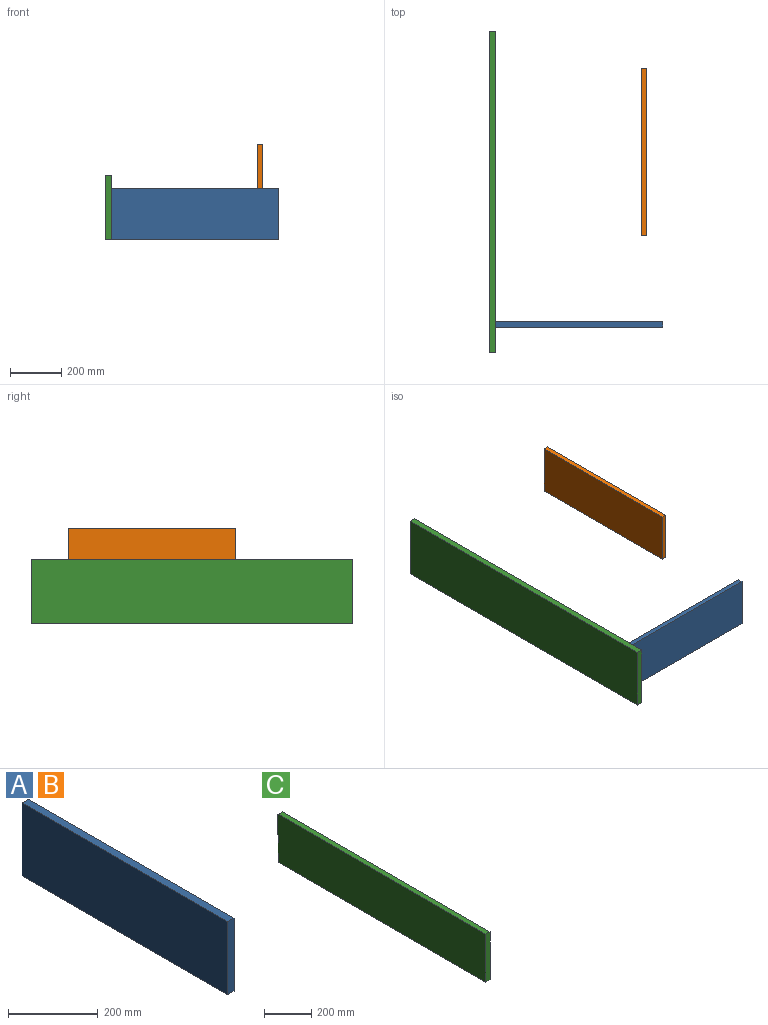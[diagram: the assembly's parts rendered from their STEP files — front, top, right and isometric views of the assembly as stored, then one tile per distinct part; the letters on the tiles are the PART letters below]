
ASSEMBLY  parts=3 mates=1
PART A: 6 faces, bbox 20x650x200 mm
  f0: plane 650x200mm, normal (-1,0,0), area 130000mm2, adj f1,f3,f4,f5
  f1: plane 650x20mm, normal (0,0,-1), area 13000mm2, adj f0,f2,f4,f5
  f2: plane 650x200mm, normal (1,0,0), area 130000mm2, adj f1,f3,f4,f5
  f3: plane 650x20mm, normal (0,0,1), area 13000mm2, adj f0,f2,f4,f5
  f4: plane 200x20mm, normal (0,1,0), area 4000mm2, adj f0,f1,f2,f3
  f5: plane 200x20mm, normal (0,-1,0), area 4000mm2, adj f0,f1,f2,f3
PART B: same geometry as A
PART C: 6 faces, bbox 25x1250x250 mm
  f0: plane 1250x250mm, normal (-1,0,0), area 312500mm2, adj f1,f3,f4,f5
  f1: plane 1250x25mm, normal (0,0,-1), area 31250mm2, adj f0,f2,f4,f5
  f2: plane 1250x250mm, normal (1,0,0), area 312500mm2, adj f1,f3,f4,f5
  f3: plane 1250x25mm, normal (0,0,1), area 31250mm2, adj f0,f2,f4,f5
  f4: plane 250x25mm, normal (0,1,0), area 6250mm2, adj f0,f1,f2,f3
  f5: plane 250x25mm, normal (0,-1,0), area 6250mm2, adj f0,f1,f2,f3
PLACE A rot(axis=(0,0,-1),90deg) t=(25,120,0)mm
PLACE B t=(592.86,455.64,170.03)mm
PLACE C at identity fixed
MATE fastened A.f5 <-> C.f2  axis (-1,0,0) through (25,100,0)mm
